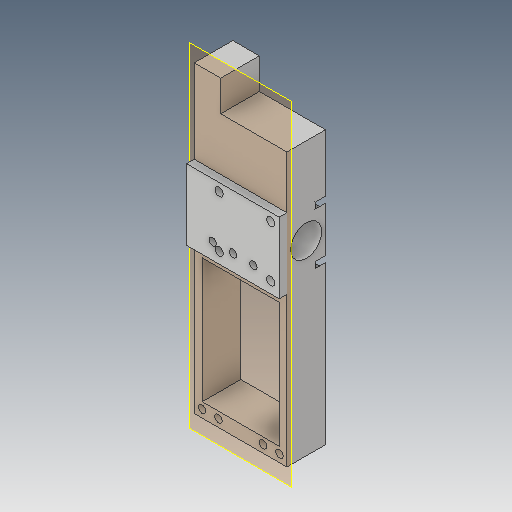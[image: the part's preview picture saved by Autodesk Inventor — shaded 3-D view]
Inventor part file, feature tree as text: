
AUTODESK INVENTOR PART (.ipt)
format: ipt  version: 2019.4 (Build 234330000, 330)  size: 205,312 bytes
history: native  units: mm
features: reference x9, sketch x5, extrude x4, other x4, projected_geometry x3, plane x2, hole x1
ambient origin geometry x8: Origin, YZ Plane, XZ Plane, XY Plane, X Axis, Y Axis, Z Axis, Center Point
bodies: Solid1 (feature_tree)
feature tree (28):
  plane  "Work Plane1"
  sketch  "Sketch1"  dims[d0=10.0mm d1=0.0mm d2=6.0mm]
  plane  "Work Plane2"
  extrude  "Extrusion1"  Depth=10.0mm
  extrude  "Extrusion2"  Depth=10.0mm TaperAngle=0.0deg
  extrude  "Extrusion3"  Depth=2.9mm
  hole  "Hole1"  [1 undecoded]
  extrude  "Extrusion4"  [1 undecoded]
  reference  "Reference1"
  sketch  "Sketch2"  dims[d3=7.5mm d4=10.0mm d5=0.0mm]
  projected_geometry  "Projected Loop1"
  reference  "Reference2"
  reference  "Reference3"
  sketch  "Sketch3"  dims[d6=2.9mm d7=2.9mm]
  reference  "Reference4"
  projected_geometry  "Projected Loop2"
  reference  "Reference5"
  sketch  "Sketch4"  dims[d8=20.0mm d9=0.0mm]
  reference  "Reference6"
  reference  "Reference7"
  reference  "Reference8"
  reference  "Reference9"
  sketch  "Sketch5"  dims[d10=3.2mm d11=6.0mm d12=7.0mm d13=4.0mm d14=90.0deg d15=8.0mm d16=20.594885mm d17=3.0mm d18=0.0mm]
  projected_geometry  "Projected Loop3"
  other  "Assembly_Opentrons_Autofocus_v1.iam"
  other  "01_Slide_camera_x_v1:1"
  other  "00_MGN12H, LINEAR GUIDE BLOCK:1"
  other  "00_spindel_slide:1"
note: 2 required parameter values undecoded (feature->parameter linkage not recoverable at this tier; creation-order binding heuristic only, values carry confidence <= 0.55)
